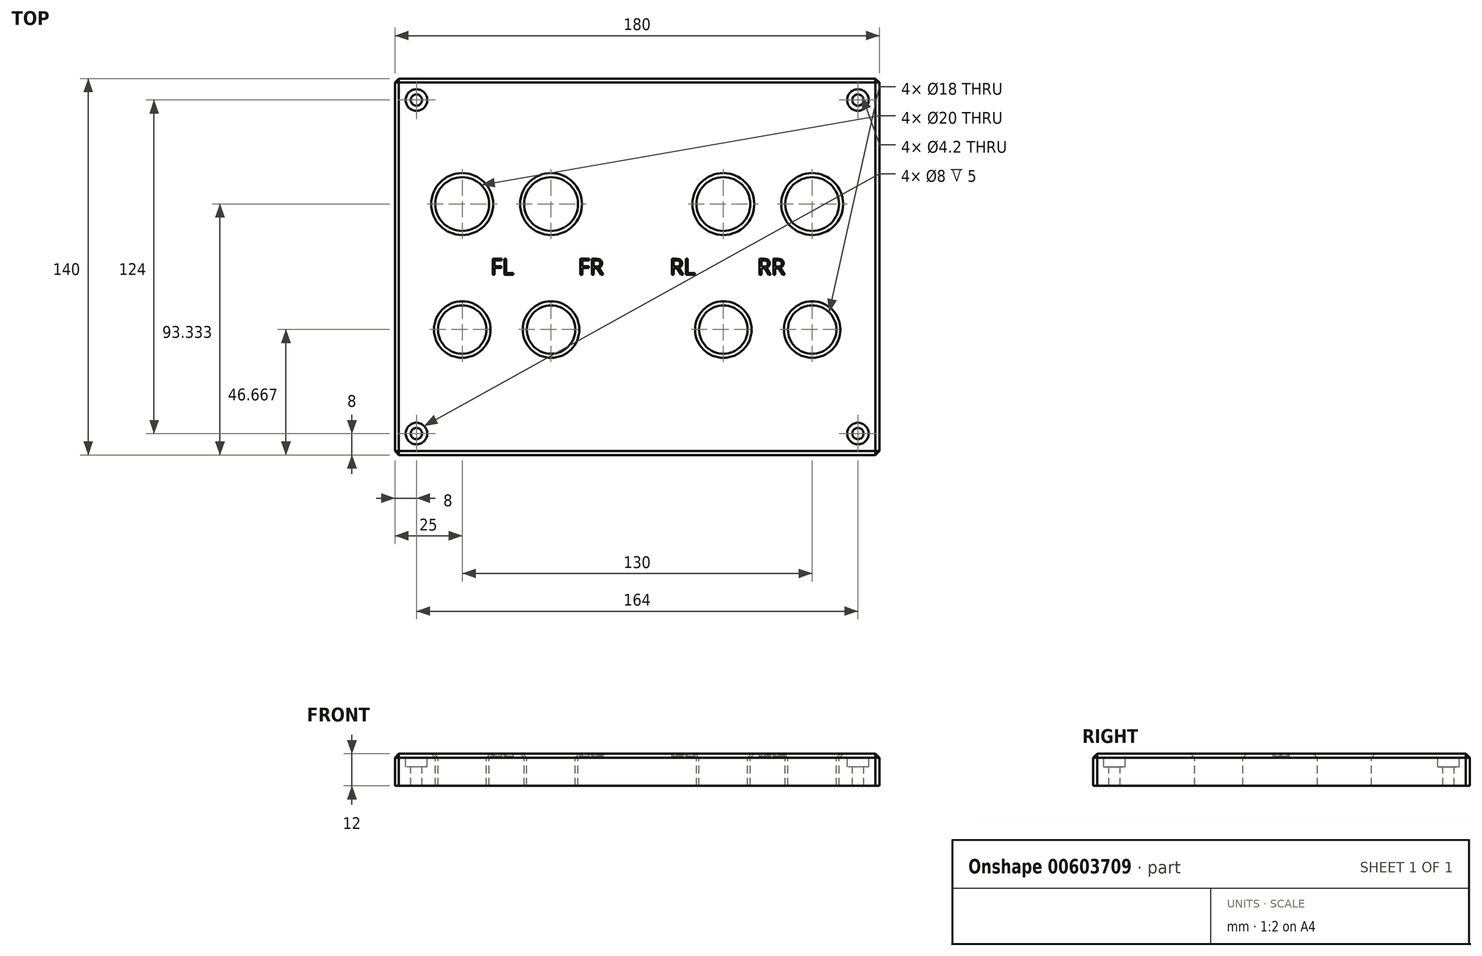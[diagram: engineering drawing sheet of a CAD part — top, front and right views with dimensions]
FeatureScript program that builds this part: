
annotation { "Feature Type Name" : "Feature", "Feature Type Description" : "" }
export const myFeature = defineFeature(function(context is Context, id is Id, definition is map)
    precondition{}
    {
        {
            var Q0;
            Q0=qCreatedBy(makeId("Top.planeOp"),FACE);
            var sketch = newSketch(context, id + "F0", { "sketchPlane" : qUnion([Q0])});
            skLineSegment(sketch, "E0.bottom", {"start": v(90, 70) * mm, "end": v(-90, 70) * mm});
            skLineSegment(sketch, "E0.top", {"start": v(90, -70) * mm, "end": v(-90, -70) * mm});
            skLineSegment(sketch, "E0.left", {"start": v(90, 70) * mm, "end": v(90, -70) * mm});
            skLineSegment(sketch, "E0.right", {"start": v(-90, 70) * mm, "end": v(-90, -70) * mm});
            skPoint(sketch, "E0.middle", {"position": v(0, 0) * mm});
            skLineSegment(sketch, "E1", {"start": v(-90, 23.33) * mm, "end": v(90, 23.33) * mm, "construction": true});
            skPoint(sketch, "E2.startSnap0", {"position": v(-90, 0) * mm});
            skPoint(sketch, "E2.endSnap0", {"position": v(90, 0) * mm});
            skCircle(sketch, "E3", {"center": v(-65, 23.33) * mm, "radius": 10 * mm});
            skCircle(sketch, "E4", {"center": v(-32, 23.33) * mm, "radius": 10 * mm});
            skCircle(sketch, "E5", {"center": v(32, 23.33) * mm, "radius": 10 * mm});
            skCircle(sketch, "E6", {"center": v(65, 23.33) * mm, "radius": 10 * mm});
            skLineSegment(sketch, "E7", {"start": v(-90, -23.33) * mm, "end": v(90, -23.33) * mm, "construction": true});
            skCircle(sketch, "E8", {"center": v(-65, -23.33) * mm, "radius": 9 * mm});
            skCircle(sketch, "E9", {"center": v(-32, -23.33) * mm, "radius": 9 * mm});
            skCircle(sketch, "E10", {"center": v(32, -23.33) * mm, "radius": 9 * mm});
            skCircle(sketch, "E11", {"center": v(65, -23.33) * mm, "radius": 9 * mm});
            skPoint(sketch, "E12", {"position": v(-82, -62) * mm});
            skPoint(sketch, "E13", {"position": v(82, -62) * mm});
            skPoint(sketch, "E14", {"position": v(82, 62) * mm});
            skPoint(sketch, "E15", {"position": v(-82, 62) * mm});
            skSolve(sketch);
        }
        {
            var Q0;
            Q0=makeQuery(id+"F0.imprint","IMPRINT",FACE,{"disambiguationData":[TD([[makeQuery(id+"F0.imprint","IMPRINT",EDGE,{"derivedFrom":sQuery(id+"F0.wireOp",EDGE,"E0.bottom")}),1.0]])]});
            extrude(context, id + "F1", {"entities" : qUnion([Q0]), "oppositeDirection" : true, "depth" : 12 * mm, "offsetDistance" : 25 * mm});
        }
        {
            var Q0;
            Q0=makeQuery(id+"F1.opExtrude","SWEPT_EDGE",EDGE,{"disambiguationData":[OSD([sQuery(id+"F0.wireOp",EDGE,"E0.bottom"),sQuery(id+"F0.wireOp",EDGE,"E0.right")])]});
            var Q1;
            Q1=makeQuery(id+"F1.opExtrude","SWEPT_EDGE",EDGE,{"disambiguationData":[OSD([sQuery(id+"F0.wireOp",EDGE,"E0.bottom"),sQuery(id+"F0.wireOp",EDGE,"E0.left")])]});
            var Q2;
            Q2=makeQuery(id+"F1.opExtrude","SWEPT_EDGE",EDGE,{"disambiguationData":[OSD([sQuery(id+"F0.wireOp",EDGE,"E0.top"),sQuery(id+"F0.wireOp",EDGE,"E0.left")])]});
            var Q3;
            Q3=makeQuery(id+"F1.opExtrude","SWEPT_EDGE",EDGE,{"disambiguationData":[OSD([sQuery(id+"F0.wireOp",EDGE,"E0.top"),sQuery(id+"F0.wireOp",EDGE,"E0.right")])]});
            var Q4;
            Q4=makeQuery(id+"F1.opExtrude","CAP_EDGE",EDGE,{"disambiguationData":[OSD([sQuery(id+"F0.wireOp",EDGE,"E0.bottom")])],"isStart":true});
            var Q5;
            Q5=makeQuery(id+"F1.opExtrude","CAP_EDGE",EDGE,{"disambiguationData":[OSD([sQuery(id+"F0.wireOp",EDGE,"E0.top")])],"isStart":true});
            var Q6;
            Q6=makeQuery(id+"F1.opExtrude","CAP_EDGE",EDGE,{"disambiguationData":[OSD([sQuery(id+"F0.wireOp",EDGE,"E0.right")])],"isStart":true});
            var Q7;
            Q7=makeQuery(id+"F1.opExtrude","CAP_EDGE",EDGE,{"disambiguationData":[OSD([sQuery(id+"F0.wireOp",EDGE,"E0.left")])],"isStart":true});
            chamfer(context, id + "F2", {"entities" : qUnion([Q0, Q1, Q2, Q3, Q4, Q5, Q6, Q7]), "width" : 1.5 * mm, "tangentPropagation" : true});
        }
        {
            var Q0;
            Q0=makeQuery(id+"F1.opExtrude","CAP_EDGE",EDGE,{"disambiguationData":[OSD([sQuery(id+"F0.wireOp",EDGE,"E3")])],"isStart":true});
            var Q1;
            Q1=makeQuery(id+"F1.opExtrude","CAP_EDGE",EDGE,{"disambiguationData":[OSD([sQuery(id+"F0.wireOp",EDGE,"E4")])],"isStart":true});
            var Q2;
            Q2=makeQuery(id+"F1.opExtrude","CAP_EDGE",EDGE,{"disambiguationData":[OSD([sQuery(id+"F0.wireOp",EDGE,"E5")])],"isStart":true});
            var Q3;
            Q3=makeQuery(id+"F1.opExtrude","CAP_EDGE",EDGE,{"disambiguationData":[OSD([sQuery(id+"F0.wireOp",EDGE,"E6")])],"isStart":true});
            var Q4;
            Q4=makeQuery(id+"F1.opExtrude","CAP_EDGE",EDGE,{"disambiguationData":[OSD([sQuery(id+"F0.wireOp",EDGE,"E8")])],"isStart":true});
            var Q5;
            Q5=makeQuery(id+"F1.opExtrude","CAP_EDGE",EDGE,{"disambiguationData":[OSD([sQuery(id+"F0.wireOp",EDGE,"E9")])],"isStart":true});
            var Q6;
            Q6=makeQuery(id+"F1.opExtrude","CAP_EDGE",EDGE,{"disambiguationData":[OSD([sQuery(id+"F0.wireOp",EDGE,"E10")])],"isStart":true});
            var Q7;
            Q7=makeQuery(id+"F1.opExtrude","CAP_EDGE",EDGE,{"disambiguationData":[OSD([sQuery(id+"F0.wireOp",EDGE,"E11")])],"isStart":true});
            chamfer(context, id + "F3", {"entities" : qUnion([Q0, Q1, Q2, Q3, Q4, Q5, Q6, Q7]), "width" : 1.5 * mm, "tangentPropagation" : true});
        }
        {
            var Q0;
            Q0=sQuery(id+"F0.wireOp",VERTEX,"E14");
            var Q1;
            Q1=sQuery(id+"F0.wireOp",VERTEX,"E13");
            var Q2;
            Q2=sQuery(id+"F0.wireOp",VERTEX,"E12");
            var Q3;
            Q3=sQuery(id+"F0.wireOp",VERTEX,"E15");
            var Q4;
            Q4=makeQuery(id+"F1.opExtrude","SWEPT_BODY",BODY,{"disambiguationData":[OSD([sQuery(id+"F0.wireOp",EDGE,"E0.bottom"),sQuery(id+"F0.wireOp",EDGE,"E0.top"),sQuery(id+"F0.wireOp",EDGE,"E0.left"),sQuery(id+"F0.wireOp",EDGE,"E0.right"),sQuery(id+"F0.wireOp",EDGE,"E3"),sQuery(id+"F0.wireOp",EDGE,"E4"),sQuery(id+"F0.wireOp",EDGE,"E5"),sQuery(id+"F0.wireOp",EDGE,"E6"),sQuery(id+"F0.wireOp",EDGE,"E8"),sQuery(id+"F0.wireOp",EDGE,"E9"),sQuery(id+"F0.wireOp",EDGE,"E10"),sQuery(id+"F0.wireOp",EDGE,"E11")])]});
            hole(context, id + "F4", {"style" : HoleStyle.C_BORE, "endStyle" : HoleEndStyle.THROUGH, "holeDiameter" : 4.2 * mm, "cBoreDiameter" : 8 * mm, "cBoreDepth" : 5 * mm, "majorDiameter" : 5 * mm, "isTappedThrough" : true, "tappedDepth" : 12 * mm, "tapClearance" : 3, "startFromSketch" : true, "locations" : qUnion([Q0, Q1, Q2, Q3]), "scope" : qUnion([Q4])});
        }
        {
            var Q0;
            Q0=qCreatedBy(makeId("Top.planeOp"),FACE);
            var sketch = newSketch(context, id + "F5", { "sketchPlane" : qUnion([Q0])});
            skLineSegment(sketch, "E16", {"start": v(-73.16, 3) * mm, "end": v(73.36, 3) * mm, "construction": true});
            skLineSegment(sketch, "E17", {"start": v(-73.16, -3) * mm, "end": v(73.36, -3) * mm, "construction": true});
            skPoint(sketch, "E18.0", {"position": v(-65, 23.33) * mm});
            skText(sketch, "E19", { "text": "FL", "fontName": "OpenSans-Regular.ttf"});
            skLineSegment(sketch, "E20", {"start": v(-65, 23.33) * mm, "end": v(-65, -3) * mm, "construction": true});
            skPoint(sketch, "E21.0", {"position": v(-32, 23.33) * mm});
            skPoint(sketch, "E22.0", {"position": v(32, 23.33) * mm});
            skPoint(sketch, "E23.0", {"position": v(65, 23.33) * mm});
            skLineSegment(sketch, "E24", {"start": v(-32, 23.33) * mm, "end": v(-32, -3) * mm, "construction": true});
            skLineSegment(sketch, "E25", {"start": v(32, 23.33) * mm, "end": v(32, -3) * mm, "construction": true});
            skLineSegment(sketch, "E26", {"start": v(65, 23.33) * mm, "end": v(65, -3) * mm, "construction": true});
            skText(sketch, "E27", { "text": "FR", "fontName": "OpenSans-Regular.ttf"});
            skText(sketch, "E28", { "text": "RL", "fontName": "OpenSans-Regular.ttf"});
            skText(sketch, "E29", { "text": "RR", "fontName": "OpenSans-Regular.ttf"});
            const initialGuessF5  = {"E19": [-0.05449, -0.003, 1, 0, 0.006], "E27": [-0.02193, -0.003, 1, 0, 0.006], "E28": [0.01209, -0.003, 1, 0, 0.006], "E29": [0.04465, -0.003, 1, 0, 0.006]};
            skSetInitialGuess(sketch, initialGuessF5);
            skSolve(sketch);
        }
        {
            var Q0;
            Q0 = qSketchRegion(id + "F5", true);
            extrude(context, id + "F6", {"entities" : qUnion([Q0]), "operationType" : NewBodyOperationType.REMOVE, "oppositeDirection" : true, "depth" : 1 * mm, "offsetDistance" : 25 * mm});
        }
    });
